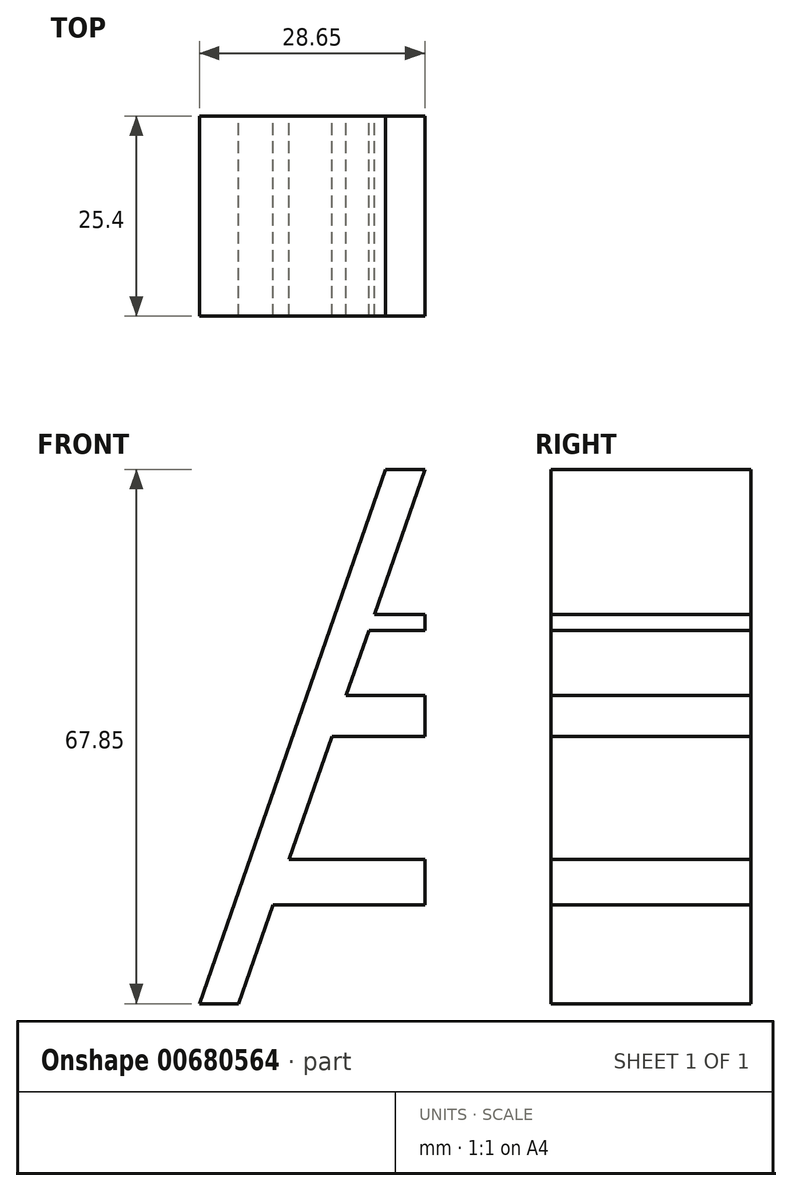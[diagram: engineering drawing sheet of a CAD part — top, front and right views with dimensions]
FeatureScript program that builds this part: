
annotation { "Feature Type Name" : "Feature", "Feature Type Description" : "" }
export const myFeature = defineFeature(function(context is Context, id is Id, definition is map)
    precondition{}
    {
        {
            var Q0;
            Q0=qCreatedBy(makeId("Front.planeOp"),FACE);
            var sketch = newSketch(context, id + "F0", { "sketchPlane" : qUnion([Q0])});
            skLineSegment(sketch, "E0", {"start": v(-23.65, 0) * mm, "end": v(0, 67.85) * mm, "construction": true});
            skLineSegment(sketch, "E1", {"start": v(-23.65, 0) * mm, "end": v(-19.27, 12.57) * mm});
            skLineSegment(sketch, "E2", {"start": v(-19.27, 12.57) * mm, "end": v(0, 12.57) * mm});
            skLineSegment(sketch, "E3", {"start": v(0, 12.57) * mm, "end": v(0, 18.33) * mm});
            skLineSegment(sketch, "E4", {"start": v(0, 18.33) * mm, "end": v(-17.26, 18.33) * mm});
            skLineSegment(sketch, "E5", {"start": v(-17.26, 18.33) * mm, "end": v(-11.82, 33.93) * mm});
            skLineSegment(sketch, "E6", {"start": v(-11.82, 33.93) * mm, "end": v(0, 33.93) * mm});
            skLineSegment(sketch, "E7", {"start": v(0, 33.93) * mm, "end": v(0, 39.13) * mm});
            skLineSegment(sketch, "E8", {"start": v(0, 39.13) * mm, "end": v(-10.01, 39.13) * mm});
            skLineSegment(sketch, "E9", {"start": v(-10.01, 39.13) * mm, "end": v(-7.12, 47.42) * mm});
            skLineSegment(sketch, "E10", {"start": v(-7.12, 47.42) * mm, "end": v(0, 47.42) * mm});
            skLineSegment(sketch, "E11", {"start": v(0, 47.42) * mm, "end": v(0, 49.42) * mm});
            skLineSegment(sketch, "E12", {"start": v(0, 49.42) * mm, "end": v(-6.42, 49.42) * mm});
            skLineSegment(sketch, "E13", {"start": v(-6.42, 49.42) * mm, "end": v(0, 67.85) * mm});
            skLineSegment(sketch, "E14", {"start": v(-5, 67.85) * mm, "end": v(-28.65, 0) * mm});
            skLineSegment(sketch, "E15", {"start": v(-28.65, 0) * mm, "end": v(-23.65, 0) * mm});
            skLineSegment(sketch, "E16", {"start": v(0, 67.85) * mm, "end": v(-5, 67.85) * mm});
            skSolve(sketch);
        }
        {
            var Q0;
            Q0=makeQuery(id+"F0.imprint","IMPRINT",FACE,{"disambiguationData":[TD([[makeQuery(id+"F0.imprint","IMPRINT",EDGE,{"derivedFrom":sQuery(id+"F0.wireOp",EDGE,"E1")}),1.0]])]});
            extrude(context, id + "F1", {"entities" : qUnion([Q0]), "depth" : 25.4 * mm, "offsetDistance" : 25.4 * mm});
        }
    });
